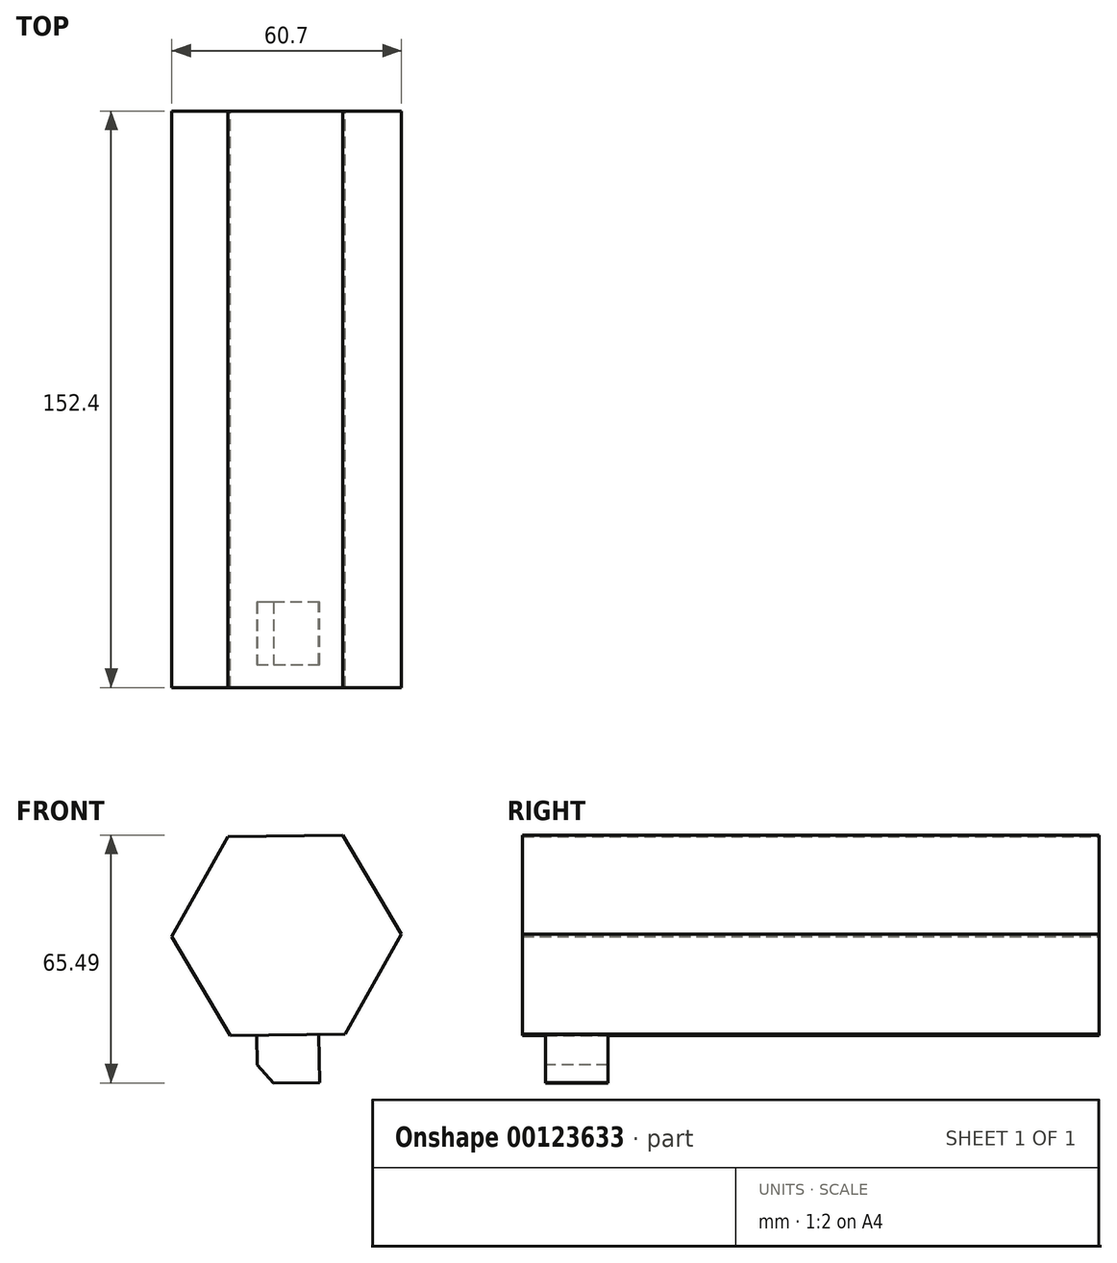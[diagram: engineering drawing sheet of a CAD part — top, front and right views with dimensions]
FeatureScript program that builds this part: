
annotation { "Feature Type Name" : "Feature", "Feature Type Description" : "" }
export const myFeature = defineFeature(function(context is Context, id is Id, definition is map)
    precondition{}
    {
        {
            var Q0;
            Q0=qCreatedBy(makeId("Front.planeOp"),FACE);
            var sketch = newSketch(context, id + "F0", { "sketchPlane" : qUnion([Q0])});
            skCircle(sketch, "E0.cCircle", {"center": v(0, 0) * mm, "radius": 26.29 * mm, "construction": true});
            skLineSegment(sketch, "E0.0", {"start": v(30.35, 0.35) * mm, "end": v(15.48, -26.11) * mm});
            skLineSegment(sketch, "E0.1", {"start": v(15.48, -26.11) * mm, "end": v(-14.87, -26.46) * mm});
            skLineSegment(sketch, "E0.2", {"start": v(-14.87, -26.46) * mm, "end": v(-30.35, -0.35) * mm});
            skLineSegment(sketch, "E0.3", {"start": v(-30.35, -0.35) * mm, "end": v(-15.48, 26.11) * mm});
            skLineSegment(sketch, "E0.4", {"start": v(-15.48, 26.11) * mm, "end": v(14.87, 26.46) * mm});
            skLineSegment(sketch, "E0.5", {"start": v(14.87, 26.46) * mm, "end": v(30.35, 0.35) * mm});
            skPoint(sketch, "E0.0.midPoint", {"position": v(22.92, -12.88) * mm});
            skSolve(sketch);
        }
        {
            var Q0;
            Q0 = qSketchRegion(id + "F0", true);
            extrude(context, id + "F1", {"entities" : qUnion([Q0]), "depth" : 152.4 * mm});
        }
        {
            var Q0;
            Q0=makeQuery(id+"F1.opExtrude","SWEPT_FACE",FACE,{"disambiguationData":[OSD([sQuery(id+"F0.wireOp",EDGE,"E0.1")])]});
            var sketch = newSketch(context, id + "F2", { "sketchPlane" : qUnion([Q0])});
            skCircle(sketch, "E1.cCircle", {"center": v(0, 138.04) * mm, "radius": 8.23 * mm, "construction": true});
            skLineSegment(sketch, "E1.0", {"start": v(8.23, 146.27) * mm, "end": v(8.23, 129.8) * mm});
            skLineSegment(sketch, "E1.1", {"start": v(8.23, 129.8) * mm, "end": v(-8.23, 129.8) * mm});
            skLineSegment(sketch, "E1.2", {"start": v(-8.23, 129.8) * mm, "end": v(-8.23, 146.27) * mm});
            skLineSegment(sketch, "E1.3", {"start": v(-8.23, 146.27) * mm, "end": v(8.23, 146.27) * mm});
            skPoint(sketch, "E1.0.midPoint", {"position": v(8.23, 138.04) * mm});
            skSolve(sketch);
        }
        {
            var Q0;
            Q0 = qSketchRegion(id + "F2", true);
            extrude(context, id + "F3", {"entities" : qUnion([Q0]), "operationType" : NewBodyOperationType.ADD, "depth" : 12.7 * mm});
        }
        {
            var Q0;
            Q0=makeQuery(id+"F3.opExtrude","SWEPT_FACE",FACE,{"disambiguationData":[OSD([sQuery(id+"F2.wireOp",EDGE,"E1.3")])]});
            var sketch = newSketch(context, id + "F4", { "sketchPlane" : qUnion([Q0])});
            skLineSegment(sketch, "E2", {"start": v(-7.83, -34.3) * mm, "end": v(-3.48, -39.03) * mm});
            skSolve(sketch);
        }
        {
            var Q0;
            {var subQ0=sQuery(id+"F4.wireOp",EDGE,"E2");Q0=makeQuery(id+"F4.imprint","IMPRINT",FACE,{"disambiguationData":[TD([[makeQuery(id+"F4.imprint","IMPRINT",EDGE,{"derivedFrom":subQ0}),-1.0]])]});}
            extrude(context, id + "F5", {"entities" : qUnion([Q0]), "operationType" : NewBodyOperationType.REMOVE, "oppositeDirection" : true, "depth" : 25.4 * mm});
        }
    });
